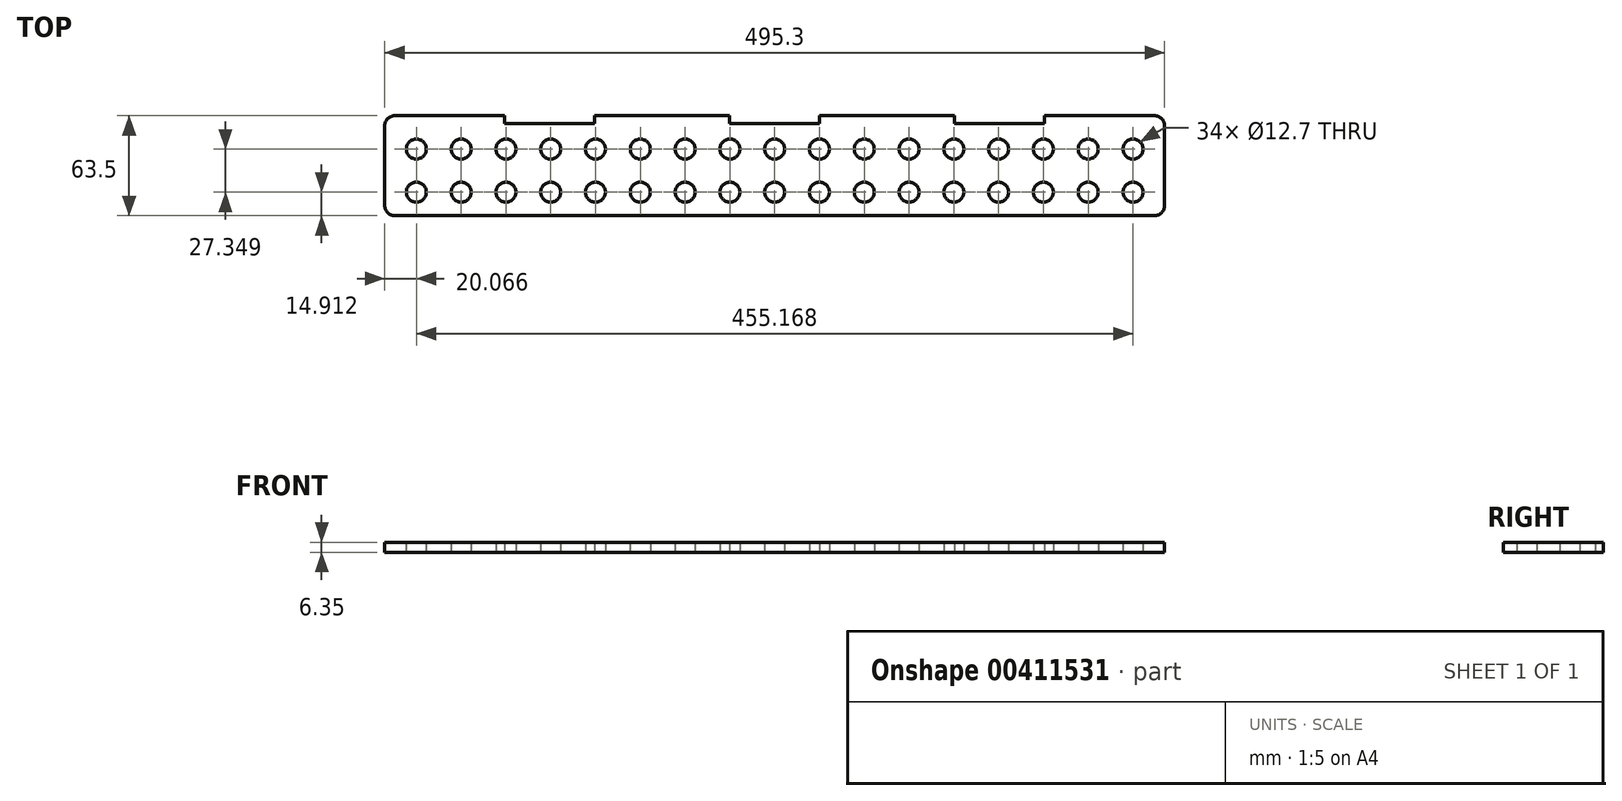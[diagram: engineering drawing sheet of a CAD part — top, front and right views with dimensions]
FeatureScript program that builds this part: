
annotation { "Feature Type Name" : "Feature", "Feature Type Description" : "" }
export const myFeature = defineFeature(function(context is Context, id is Id, definition is map)
    precondition{}
    {
        {
            var Q0;
            Q0=qCreatedBy(makeId("Top.planeOp"),FACE);
            var sketch = newSketch(context, id + "F0", { "sketchPlane" : qUnion([Q0])});
            skLineSegment(sketch, "E0.bottom", {"start": v(6.35, 0) * mm, "end": v(76.2, 0) * mm});
            skLineSegment(sketch, "E0.top", {"start": v(6.35, -63.5) * mm, "end": v(488.95, -63.5) * mm});
            skLineSegment(sketch, "E0.left", {"start": v(0, -6.35) * mm, "end": v(0, -57.15) * mm});
            skLineSegment(sketch, "E0.right", {"start": v(495.3, -6.35) * mm, "end": v(495.3, -57.15) * mm});
            skCircle(sketch, "E1", {"center": v(20.07, -21.24) * mm, "radius": 6.35 * mm});
            skCircle(sketch, "E2", {"center": v(20.07, -48.59) * mm, "radius": 6.35 * mm});
            skCircle(sketch, "E3.1.0.0", {"center": v(48.51, -48.59) * mm, "radius": 6.35 * mm});
            skCircle(sketch, "E3.1.0.3", {"center": v(48.51, -21.24) * mm, "radius": 6.35 * mm});
            skCircle(sketch, "E3.2.0.0", {"center": v(76.96, -48.59) * mm, "radius": 6.35 * mm});
            skCircle(sketch, "E3.2.0.3", {"center": v(76.96, -21.24) * mm, "radius": 6.35 * mm});
            skCircle(sketch, "E3.3.0.0", {"center": v(105.41, -48.59) * mm, "radius": 6.35 * mm});
            skCircle(sketch, "E3.3.0.3", {"center": v(105.41, -21.24) * mm, "radius": 6.35 * mm});
            skCircle(sketch, "E3.4.0.0", {"center": v(133.86, -48.59) * mm, "radius": 6.35 * mm});
            skCircle(sketch, "E3.4.0.3", {"center": v(133.86, -21.24) * mm, "radius": 6.35 * mm});
            skCircle(sketch, "E3.5.0.0", {"center": v(162.3, -48.59) * mm, "radius": 6.35 * mm});
            skCircle(sketch, "E3.5.0.3", {"center": v(162.3, -21.24) * mm, "radius": 6.35 * mm});
            skCircle(sketch, "E3.6.0.0", {"center": v(190.75, -48.59) * mm, "radius": 6.35 * mm});
            skCircle(sketch, "E3.6.0.3", {"center": v(190.75, -21.24) * mm, "radius": 6.35 * mm});
            skCircle(sketch, "E3.7.0.0", {"center": v(219.2, -48.59) * mm, "radius": 6.35 * mm});
            skCircle(sketch, "E3.7.0.3", {"center": v(219.2, -21.24) * mm, "radius": 6.35 * mm});
            skCircle(sketch, "E3.8.0.0", {"center": v(247.65, -48.59) * mm, "radius": 6.35 * mm});
            skCircle(sketch, "E3.8.0.3", {"center": v(247.65, -21.24) * mm, "radius": 6.35 * mm});
            skCircle(sketch, "E3.9.0.0", {"center": v(276.1, -48.59) * mm, "radius": 6.35 * mm});
            skCircle(sketch, "E3.9.0.3", {"center": v(276.1, -21.24) * mm, "radius": 6.35 * mm});
            skCircle(sketch, "E3.10.0.0", {"center": v(304.55, -48.59) * mm, "radius": 6.35 * mm});
            skCircle(sketch, "E3.10.0.3", {"center": v(304.55, -21.24) * mm, "radius": 6.35 * mm});
            skCircle(sketch, "E3.11.0.0", {"center": v(333, -48.59) * mm, "radius": 6.35 * mm});
            skCircle(sketch, "E3.11.0.3", {"center": v(333, -21.24) * mm, "radius": 6.35 * mm});
            skCircle(sketch, "E3.12.0.0", {"center": v(361.44, -48.59) * mm, "radius": 6.35 * mm});
            skCircle(sketch, "E3.12.0.3", {"center": v(361.44, -21.24) * mm, "radius": 6.35 * mm});
            skCircle(sketch, "E3.13.0.0", {"center": v(389.9, -48.59) * mm, "radius": 6.35 * mm});
            skCircle(sketch, "E3.13.0.3", {"center": v(389.9, -21.24) * mm, "radius": 6.35 * mm});
            skCircle(sketch, "E3.14.0.0", {"center": v(418.34, -48.59) * mm, "radius": 6.35 * mm});
            skCircle(sketch, "E3.14.0.3", {"center": v(418.34, -21.24) * mm, "radius": 6.35 * mm});
            skCircle(sketch, "E3.15.0.0", {"center": v(446.79, -48.59) * mm, "radius": 6.35 * mm});
            skCircle(sketch, "E3.15.0.3", {"center": v(446.79, -21.24) * mm, "radius": 6.35 * mm});
            skCircle(sketch, "E3.16.0.0", {"center": v(475.23, -48.59) * mm, "radius": 6.35 * mm});
            skCircle(sketch, "E3.16.0.3", {"center": v(475.23, -21.24) * mm, "radius": 6.35 * mm});
            skLineSegment(sketch, "E3.direction1", {"start": v(20.07, -48.59) * mm, "end": v(48.51, -48.59) * mm, "construction": true});
            skLineSegment(sketch, "E4", {"start": v(247.65, 0) * mm, "end": v(247.65, -63.5) * mm, "construction": true});
            skPoint(sketch, "E5.visualSharp", {"position": v(0, 0) * mm});
            skArc(sketch, "E5.filletArc", {"start": v(6.35, 0) * mm, "mid": v(1.86, -1.86) * mm, "end": v(0, -6.35) * mm});
            skPoint(sketch, "E6.visualSharp", {"position": v(0, -63.5) * mm});
            skArc(sketch, "E6.filletArc", {"start": v(0, -57.15) * mm, "mid": v(1.86, -61.64) * mm, "end": v(6.35, -63.5) * mm});
            skPoint(sketch, "E7.visualSharp", {"position": v(495.3, -63.5) * mm});
            skArc(sketch, "E7.filletArc", {"start": v(488.95, -63.5) * mm, "mid": v(493.44, -61.64) * mm, "end": v(495.3, -57.15) * mm});
            skPoint(sketch, "E8.visualSharp", {"position": v(495.3, 0) * mm});
            skArc(sketch, "E8.filletArc", {"start": v(495.3, -6.35) * mm, "mid": v(493.44, -1.86) * mm, "end": v(488.95, 0) * mm});
            skLineSegment(sketch, "E9", {"start": v(123.83, 0) * mm, "end": v(123.83, -63.5) * mm, "construction": true});
            skLineSegment(sketch, "E10.top", {"start": v(76.2, -5.08) * mm, "end": v(133.35, -5.08) * mm});
            skLineSegment(sketch, "E10.left", {"start": v(76.2, 0) * mm, "end": v(76.2, -5.08) * mm});
            skLineSegment(sketch, "E10.right", {"start": v(133.35, 0) * mm, "end": v(133.35, -5.08) * mm});
            skLineSegment(sketch, "E11.top", {"start": v(219.07, -5.08) * mm, "end": v(276.23, -5.08) * mm});
            skLineSegment(sketch, "E11.left", {"start": v(219.07, 0) * mm, "end": v(219.07, -5.08) * mm});
            skLineSegment(sketch, "E11.right", {"start": v(276.23, 0) * mm, "end": v(276.23, -5.08) * mm});
            skLineSegment(sketch, "E12.trimOffspring", {"start": v(133.35, 0) * mm, "end": v(219.07, 0) * mm});
            skLineSegment(sketch, "E13.trimOffspring", {"start": v(276.23, 0) * mm, "end": v(361.95, 0) * mm});
            skLineSegment(sketch, "E14.MirrorCS", {"start": v(361.95, 0) * mm, "end": v(361.95, -5.08) * mm});
            skLineSegment(sketch, "E15.MirrorCS", {"start": v(419.1, 0) * mm, "end": v(419.1, -5.08) * mm});
            skLineSegment(sketch, "E16.MirrorCS", {"start": v(419.1, -5.08) * mm, "end": v(361.95, -5.08) * mm});
            skLineSegment(sketch, "E17.trimOffspring", {"start": v(419.1, 0) * mm, "end": v(488.95, 0) * mm});
            skSolve(sketch);
        }
        {
            var Q0;
            Q0=makeQuery(id+"F0.imprint","IMPRINT",FACE,{"disambiguationData":[TD([[makeQuery(id+"F0.imprint","IMPRINT",EDGE,{"derivedFrom":sQuery(id+"F0.wireOp",EDGE,"E0.bottom")}),-1.0]])]});
            extrude(context, id + "F1", {"entities" : qUnion([Q0]), "depth" : 6.35 * mm});
        }
    });
